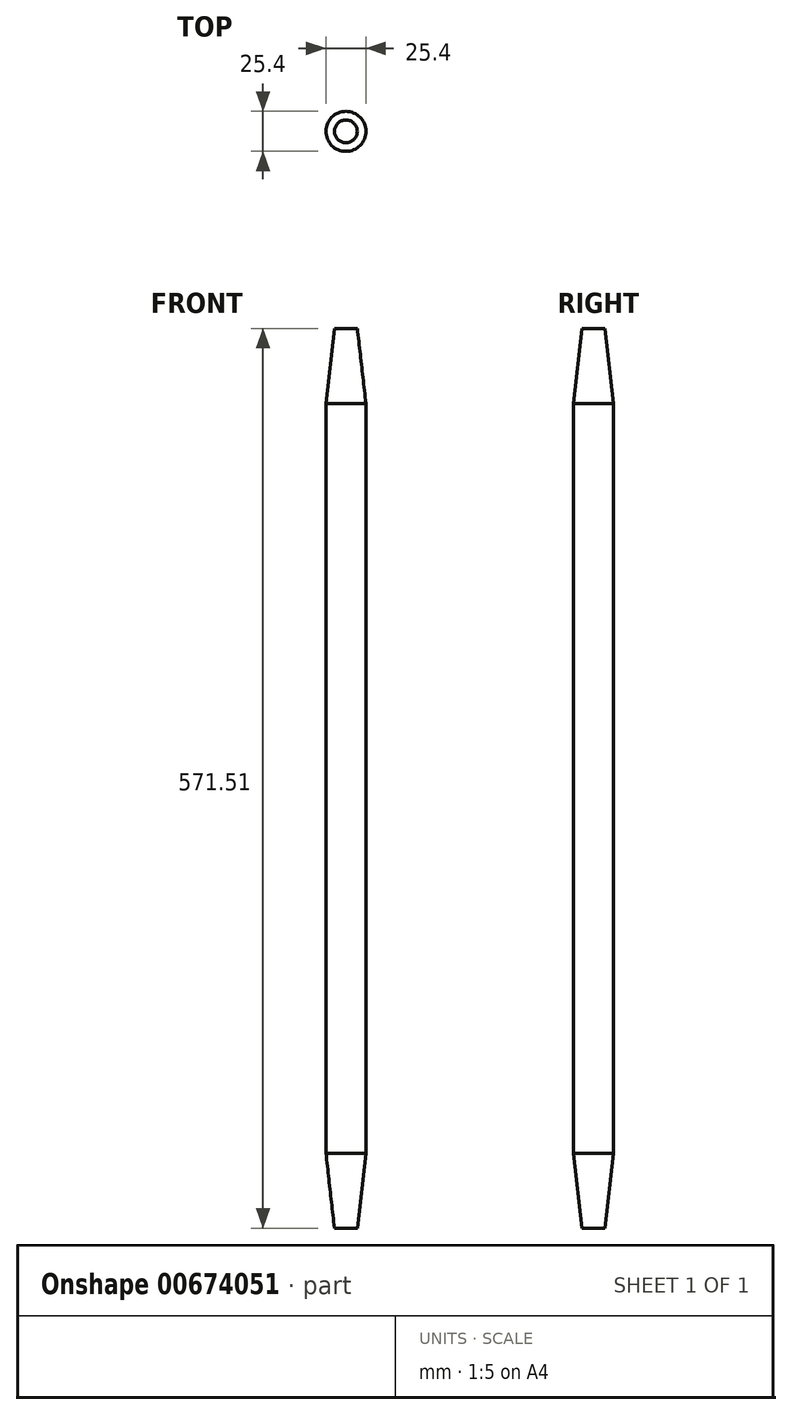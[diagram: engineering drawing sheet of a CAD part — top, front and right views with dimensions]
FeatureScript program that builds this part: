
annotation { "Feature Type Name" : "Feature", "Feature Type Description" : "" }
export const myFeature = defineFeature(function(context is Context, id is Id, definition is map)
    precondition{}
    {
        {
            var Q0;
            Q0=qCreatedBy(makeId("Top.planeOp"),FACE);
            var sketch = newSketch(context, id + "F0", { "sketchPlane" : qUnion([Q0])});
            skCircle(sketch, "E0", {"center": v(0, 0) * mm, "radius": 12.7 * mm});
            skSolve(sketch);
        }
        {
            var Q0;
            Q0 = qSketchRegion(id + "F0", true);
            extrude(context, id + "F1", {"entities" : qUnion([Q0]), "depth" : 476.25 * mm, "offsetDistance" : 25.4 * mm});
        }
        {
            var Q0;
            Q0=makeQuery(id+"F1.opExtrude","CAP_FACE",FACE,{"disambiguationData":[OSD([sQuery(id+"F0.wireOp",EDGE,"E0")])],"isStart":false});
            var sketch = newSketch(context, id + "F2", { "sketchPlane" : qUnion([Q0])});
            skCircle(sketch, "E1", {"center": v(0, 0) * mm, "radius": 12.7 * mm});
            skSolve(sketch);
        }
        {
            var Q0;
            Q0=makeQuery(id+"F2.imprint","IMPRINT",FACE,{"disambiguationData":[TD([[makeQuery(id+"F2.imprint","IMPRINT",EDGE,{"derivedFrom":sQuery(id+"F2.wireOp",EDGE,"E1")}),1.0]])]});
            extrude(context, id + "F3", {"entities" : qUnion([Q0]), "operationType" : NewBodyOperationType.ADD, "depth" : 47.62 * mm, "offsetDistance" : 25.4 * mm});
        }
        {
            var Q0;
            Q0=makeQuery(id+"F3.opExtrude","CAP_EDGE",EDGE,{"disambiguationData":[OSD([sQuery(id+"F2.wireOp",EDGE,"E1")])],"isStart":false});
            chamfer(context, id + "F4", {"entities" : qUnion([Q0]), "chamferType" : ChamferType.TWO_OFFSETS, "width1" : 5.46 * mm, "oppositeDirection" : false, "width2" : 47.62 * mm, "tangentPropagation" : true});
        }
        {
            var Q0;
            Q0=makeQuery(id+"F1.opExtrude","CAP_FACE",FACE,{"disambiguationData":[OSD([sQuery(id+"F0.wireOp",EDGE,"E0")])],"isStart":true});
            var sketch = newSketch(context, id + "F5", { "sketchPlane" : qUnion([Q0])});
            skCircle(sketch, "E2", {"center": v(0, 0) * mm, "radius": 12.7 * mm});
            skSolve(sketch);
        }
        {
            var Q0;
            Q0=makeQuery(id+"F5.imprint","IMPRINT",FACE,{"disambiguationData":[TD([[makeQuery(id+"F5.imprint","IMPRINT",EDGE,{"derivedFrom":sQuery(id+"F5.wireOp",EDGE,"E2")}),-1.0]])]});
            extrude(context, id + "F6", {"entities" : qUnion([Q0]), "operationType" : NewBodyOperationType.ADD, "depth" : 47.62 * mm, "offsetDistance" : 25.4 * mm});
        }
        {
            var Q0;
            Q0=makeQuery(id+"F6.opExtrude","CAP_EDGE",EDGE,{"disambiguationData":[OSD([sQuery(id+"F5.wireOp",EDGE,"E2")])],"isStart":false});
            chamfer(context, id + "F7", {"entities" : qUnion([Q0]), "chamferType" : ChamferType.TWO_OFFSETS, "width1" : 5.46 * mm, "oppositeDirection" : true, "width2" : 47.62 * mm, "tangentPropagation" : true});
        }
    });
